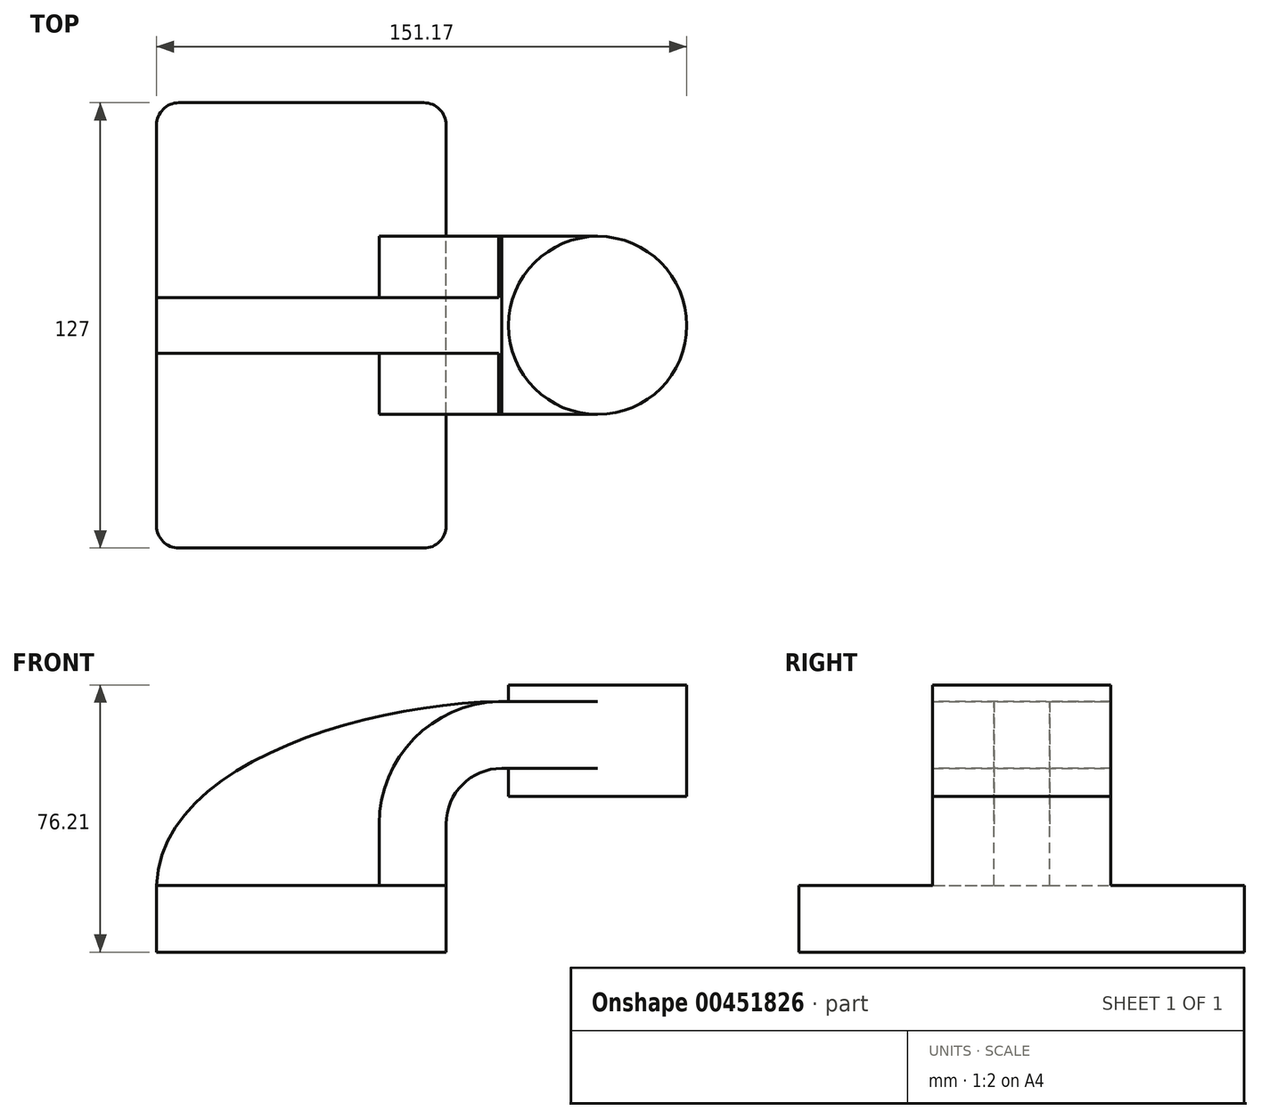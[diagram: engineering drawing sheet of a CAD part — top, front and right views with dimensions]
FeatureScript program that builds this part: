
annotation { "Feature Type Name" : "Feature", "Feature Type Description" : "" }
export const myFeature = defineFeature(function(context is Context, id is Id, definition is map)
    precondition{}
    {
        {
            var Q0;
            Q0=qCreatedBy(makeId("Front.planeOp"),FACE);
            var sketch = newSketch(context, id + "F0", { "sketchPlane" : qUnion([Q0])});
            skLineSegment(sketch, "E0.bottom", {"start": v(41.28, -9.52) * mm, "end": v(-41.28, -9.53) * mm});
            skLineSegment(sketch, "E0.top", {"start": v(41.28, 9.53) * mm, "end": v(-41.28, 9.52) * mm});
            skLineSegment(sketch, "E0.left", {"start": v(41.28, -9.52) * mm, "end": v(41.28, 9.53) * mm});
            skLineSegment(sketch, "E0.right", {"start": v(-41.28, -9.53) * mm, "end": v(-41.28, 9.52) * mm});
            skPoint(sketch, "E0.middle", {"position": v(0, 0) * mm});
            skLineSegment(sketch, "E1.bottom", {"start": v(109.89, 66.68) * mm, "end": v(59.09, 66.68) * mm});
            skLineSegment(sketch, "E1.top", {"start": v(109.89, 34.93) * mm, "end": v(59.09, 34.93) * mm});
            skLineSegment(sketch, "E1.left", {"start": v(109.89, 66.68) * mm, "end": v(109.89, 34.93) * mm});
            skLineSegment(sketch, "E1.right", {"start": v(59.09, 66.68) * mm, "end": v(59.09, 34.93) * mm});
            skPoint(sketch, "E1.middle", {"position": v(84.49, 50.8) * mm});
            skLineSegment(sketch, "E2", {"start": v(41.28, 9.53) * mm, "end": v(41.28, 27) * mm});
            skArc(sketch, "E3", {"start": v(41.28, 27) * mm, "mid": v(45.92, 38.23) * mm, "end": v(57.15, 42.88) * mm});
            skLineSegment(sketch, "E4", {"start": v(57.15, 42.88) * mm, "end": v(87.17, 42.88) * mm});
            skLineSegment(sketch, "E5.0", {"start": v(57.15, 61.93) * mm, "end": v(85.34, 61.93) * mm});
            skArc(sketch, "E5.1", {"start": v(22.23, 27) * mm, "mid": v(32.45, 51.7) * mm, "end": v(57.15, 61.93) * mm});
            skLineSegment(sketch, "E5.2", {"start": v(22.23, 9.53) * mm, "end": v(22.23, 27) * mm});
            skLineSegment(sketch, "E6", {"start": v(84.49, 50.8) * mm, "end": v(84.49, 66.68) * mm});
            skFitSpline(sketch, "E7", {"points": [v(-41.28, 9.52) * mm, v(57.15, 61.93) * mm], "startDerivative": vector(2.82, 104.38) * mm, "endDerivative": vector(115.02, 1.17) * mm});
            skLineSegment(sketch, "E8", {"start": v(84.49, 50.8) * mm, "end": v(84.49, 34.93) * mm});
            skSolve(sketch);
        }
        {
            var Q0;
            Q0=makeQuery(id+"F0.imprint","IMPRINT",FACE,{"disambiguationData":[TD([[makeQuery(id+"F0.imprint","IMPRINT",EDGE,{"derivedFrom":sQuery(id+"F0.wireOp",EDGE,"E0.bottom")}),-1.0]])]});
            extrude(context, id + "F1", {"entities" : qUnion([Q0]), "endBound" : BoundingType.SYMMETRIC, "depth" : 127 * mm});
        }
        {
            var Q0;
            {var subQ6=sQuery(id+"F0.wireOp",EDGE,"E2");Q0=makeQuery(id+"F0.imprint","IMPRINT",FACE,{"disambiguationData":[TD([[makeQuery(id+"F0.imprint","IMPRINT",EDGE,{"derivedFrom":subQ6}),1.0]])]});}
            var Q1;
            {var subQ3=sQuery(id+"F0.wireOp",EDGE,"E5.0");var subQ5=sQuery(id+"F0.wireOp",EDGE,"E1.right");var subQ6=makeQuery(id+"F0.imprint","INTERSECT",VERTEX,{"derivedFrom":[subQ5,subQ3]});Q1=makeQuery(id+"F0.imprint","IMPRINT",FACE,{"disambiguationData":[TD([[makeQuery(id+"F0.imprint","IMPRINT",EDGE,{"disambiguationData":[TD([[subQ6,-1.0]])],"derivedFrom":subQ5}),1.0]])]});}
            extrude(context, id + "F2", {"entities" : qUnion([Q0, Q1]), "operationType" : NewBodyOperationType.ADD, "endBound" : BoundingType.SYMMETRIC, "depth" : 50.8 * mm});
        }
        {
            var Q0;
            {var subQ3=sQuery(id+"F0.wireOp",EDGE,"E5.2");Q0=makeQuery(id+"F0.imprint","IMPRINT",FACE,{"disambiguationData":[TD([[makeQuery(id+"F0.imprint","IMPRINT",EDGE,{"derivedFrom":subQ3}),1.0]])]});}
            extrude(context, id + "F3", {"entities" : qUnion([Q0]), "operationType" : NewBodyOperationType.ADD, "endBound" : BoundingType.SYMMETRIC, "depth" : 15.88 * mm});
        }
        {
            var Q0;
            {var subQ0=sQuery(id+"F0.wireOp",EDGE,"E1.left");Q0=makeQuery(id+"F0.imprint","IMPRINT",FACE,{"disambiguationData":[TD([[makeQuery(id+"F0.imprint","IMPRINT",EDGE,{"derivedFrom":subQ0}),-1.0]])]});}
            var Q1;
            Q1=sQuery(id+"F0.wireOp",EDGE,"E8");
            revolve(context, id + "F4", {"operationType" : NewBodyOperationType.ADD, "entities" : qUnion([Q0]), "axis" : qUnion([Q1]), "revolveType" : RevolveType.FULL});
        }
        {
            var Q0;
            Q0=makeQuery(id+"F1.opExtrude","CAP_EDGE",EDGE,{"disambiguationData":[OSD([sQuery(id+"F0.wireOp",EDGE,"E0.left")])],"isStart":false});
            var Q1;
            Q1=makeQuery(id+"F1.opExtrude","CAP_EDGE",EDGE,{"disambiguationData":[OSD([sQuery(id+"F0.wireOp",EDGE,"E0.right")])],"isStart":false});
            var Q2;
            Q2=makeQuery(id+"F1.opExtrude","CAP_EDGE",EDGE,{"disambiguationData":[OSD([sQuery(id+"F0.wireOp",EDGE,"E0.left")])],"isStart":true});
            var Q3;
            Q3=makeQuery(id+"F1.opExtrude","CAP_EDGE",EDGE,{"disambiguationData":[OSD([sQuery(id+"F0.wireOp",EDGE,"E0.right")])],"isStart":true});
            fillet(context, id + "F5", {"entities" : qUnion([Q0, Q1, Q2, Q3]), "radius" : 6.35 * mm, "tangentPropagation" : true, "allowEdgeOverflow" : false});
        }
    });
